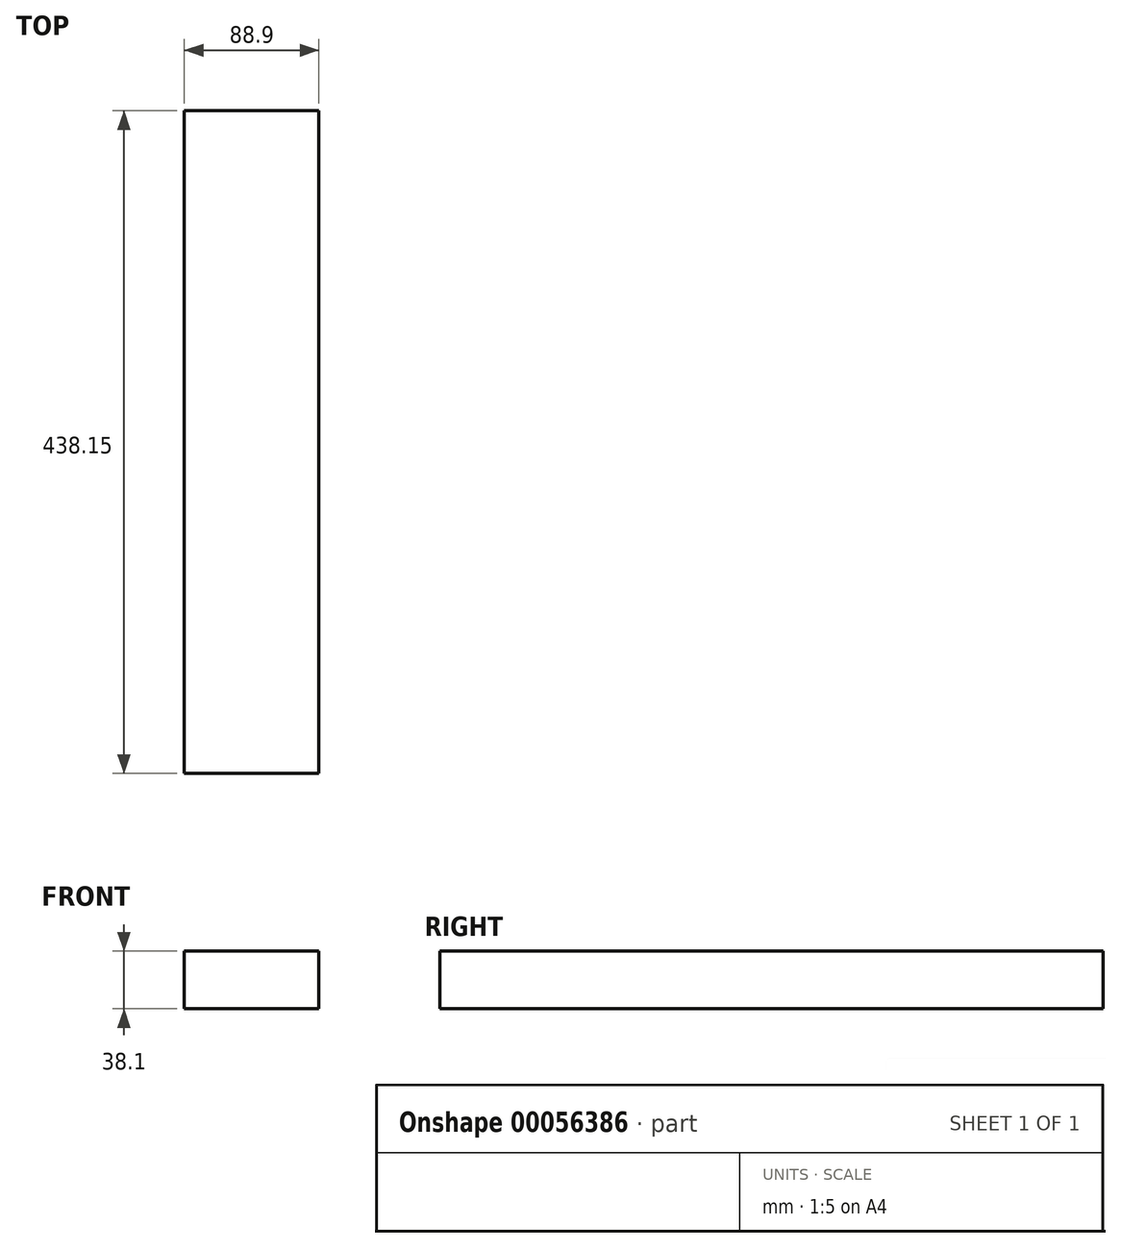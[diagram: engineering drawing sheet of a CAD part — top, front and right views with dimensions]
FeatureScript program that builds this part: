
annotation { "Feature Type Name" : "Feature", "Feature Type Description" : "" }
export const myFeature = defineFeature(function(context is Context, id is Id, definition is map)
    precondition{}
    {
        {
            var Q0;
            Q0=qCreatedBy(makeId("Front.planeOp"),FACE);
            var sketch = newSketch(context, id + "F0", { "sketchPlane" : qUnion([Q0])});
            skLineSegment(sketch, "E0.bottom", {"start": v(0, 0) * mm, "end": v(-88.9, 0) * mm});
            skLineSegment(sketch, "E0.top", {"start": v(0, 38.1) * mm, "end": v(-88.9, 38.1) * mm});
            skLineSegment(sketch, "E0.left", {"start": v(0, 0) * mm, "end": v(0, 38.1) * mm});
            skLineSegment(sketch, "E0.right", {"start": v(-88.9, 0) * mm, "end": v(-88.9, 38.1) * mm});
            skSolve(sketch);
        }
        {
            var Q0;
            Q0=makeQuery(id+"F0.imprint","IMPRINT",FACE,{"disambiguationData":[TD([[makeQuery(id+"F0.imprint","IMPRINT",EDGE,{"derivedFrom":sQuery(id+"F0.wireOp",EDGE,"E0.bottom")}),-1.0]])]});
            extrude(context, id + "F1", {"entities" : qUnion([Q0]), "depth" : 438.15 * mm});
        }
    });
